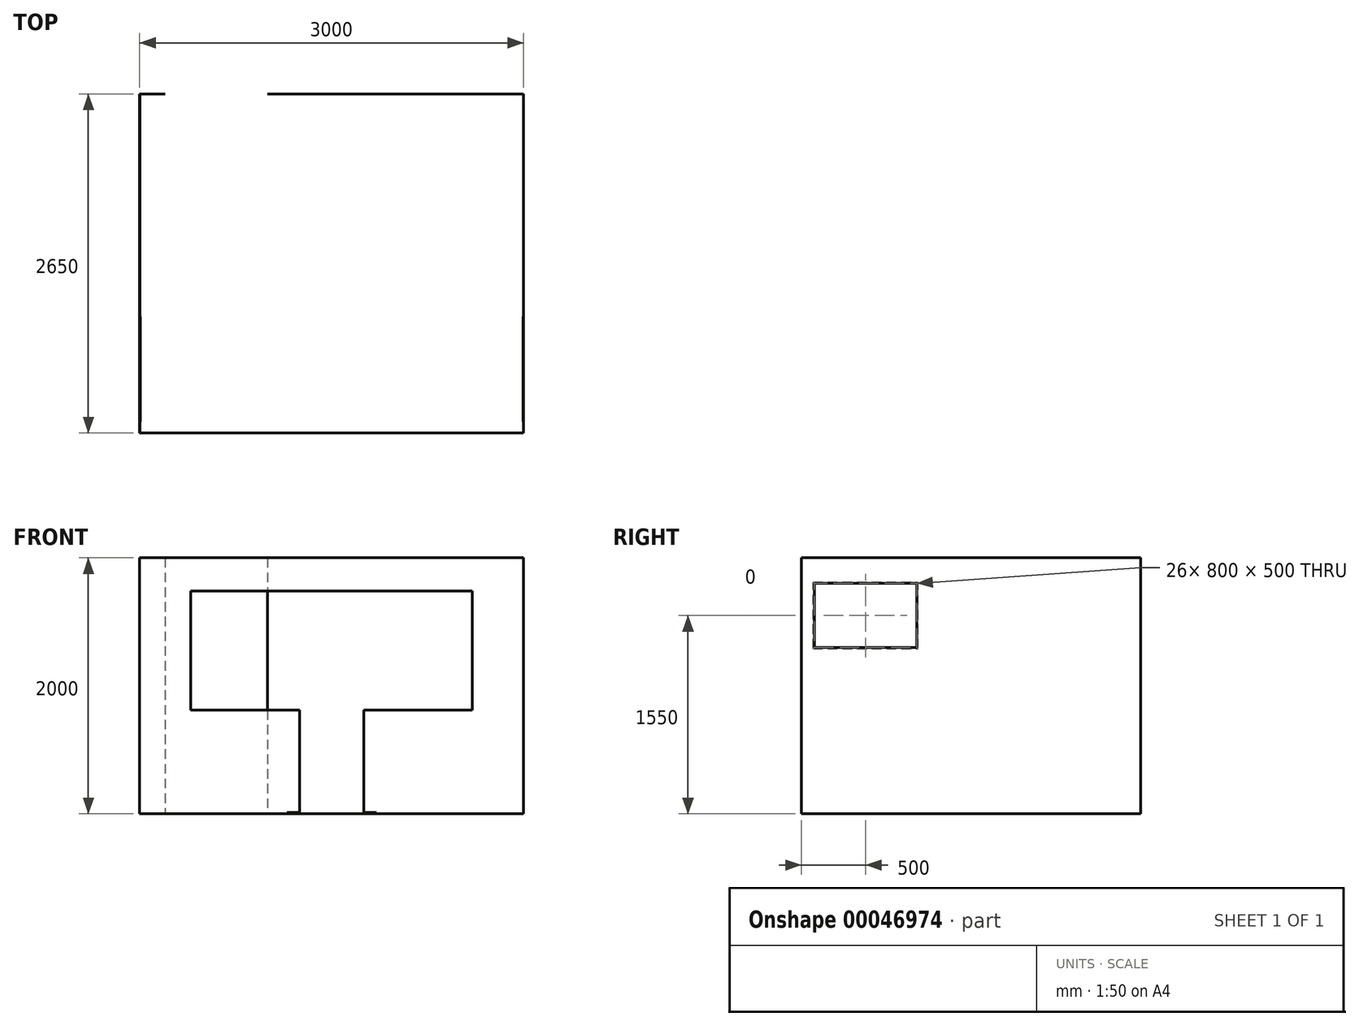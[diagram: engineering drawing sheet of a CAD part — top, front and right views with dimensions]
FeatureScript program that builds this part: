
annotation { "Feature Type Name" : "Feature", "Feature Type Description" : "" }
export const myFeature = defineFeature(function(context is Context, id is Id, definition is map)
    precondition{}
    {
        {
            var Q0;
            Q0=qCreatedBy(makeId("Top.planeOp"),FACE);
            var sketch = newSketch(context, id + "F0", { "sketchPlane" : qUnion([Q0])});
            skLineSegment(sketch, "E0.rect.bottom", {"start": v(-1500, 1325) * mm, "end": v(1500, 1325) * mm});
            skLineSegment(sketch, "E0.rect.top", {"start": v(-1500, -1325) * mm, "end": v(1500, -1325) * mm});
            skLineSegment(sketch, "E0.rect.left", {"start": v(-1500, 1325) * mm, "end": v(-1500, -1325) * mm});
            skLineSegment(sketch, "E0.rect.right", {"start": v(1500, 1325) * mm, "end": v(1500, -1325) * mm});
            skPoint(sketch, "E0.rect.middle", {"position": v(0, 0) * mm});
            skLineSegment(sketch, "E1.0", {"start": v(-1498, 1323) * mm, "end": v(-1498, -1323) * mm});
            skLineSegment(sketch, "E1.1", {"start": v(-1498, 1323) * mm, "end": v(1498, 1323) * mm});
            skLineSegment(sketch, "E1.2", {"start": v(1498, 1323) * mm, "end": v(1498, -1323) * mm});
            skLineSegment(sketch, "E1.3", {"start": v(-1498, -1323) * mm, "end": v(1498, -1323) * mm});
            skLineSegment(sketch, "E2", {"start": v(0, 1323) * mm, "end": v(0, -1323) * mm, "construction": true});
            skSolve(sketch);
        }
        {
            var Q0;
            Q0=qSketchRegion(id+"F0",true);
            extrude(context, id + "F1", {"entities" : qUnion([Q0]), "depth" : 2000 * mm});
        }
        {
            var Q0;
            Q0=makeQuery(id+"F1.opExtrude","SWEPT_FACE",FACE,{"disambiguationData":[OSD([sQuery(id+"F0.wireOp",EDGE,"E0.rect.top")])]});
            var sketch = newSketch(context, id + "F2", { "sketchPlane" : qUnion([Q0])});
            skLineSegment(sketch, "E3", {"start": v(0, 0) * mm, "end": v(0, 1740) * mm, "construction": true});
            skLineSegment(sketch, "E4", {"start": v(0, 1740) * mm, "end": v(-1100, 1740) * mm});
            skLineSegment(sketch, "E5", {"start": v(-1100, 0) * mm, "end": v(0, 0) * mm});
            skLineSegment(sketch, "E6.MirrorCS", {"start": v(1100, 0) * mm, "end": v(0, 0) * mm});
            skLineSegment(sketch, "E7.MirrorCS", {"start": v(0, 1740) * mm, "end": v(1100, 1740) * mm});
            skLineSegment(sketch, "E8", {"start": v(-1100, 810) * mm, "end": v(-350, 810) * mm});
            skLineSegment(sketch, "E9", {"start": v(-1100, 810) * mm, "end": v(-1100, 1740) * mm});
            skLineSegment(sketch, "E10.MirrorCS", {"start": v(1100, 810) * mm, "end": v(1100, 1740) * mm});
            skLineSegment(sketch, "E11", {"start": v(350, 10) * mm, "end": v(250, 10) * mm});
            skLineSegment(sketch, "E12", {"start": v(250, 10) * mm, "end": v(250, 810) * mm});
            skLineSegment(sketch, "E13", {"start": v(350, 10) * mm, "end": v(350, 0) * mm});
            skLineSegment(sketch, "E14.MirrorCS", {"start": v(-350, 10) * mm, "end": v(-350, 0) * mm});
            skLineSegment(sketch, "E15.MirrorCS", {"start": v(-350, 810) * mm, "end": v(-250, 810) * mm});
            skLineSegment(sketch, "E16.MirrorCS", {"start": v(-250, 10) * mm, "end": v(-250, 810) * mm});
            skLineSegment(sketch, "E17.MirrorCS", {"start": v(-350, 10) * mm, "end": v(-250, 10) * mm});
            skLineSegment(sketch, "E18", {"start": v(1100, 810) * mm, "end": v(250, 810) * mm});
            skSolve(sketch);
        }
        {
            var Q0;
            Q0=qSketchRegion(id+"F2",true);
            extrude(context, id + "F3", {"entities" : qUnion([Q0]), "operationType" : NewBodyOperationType.REMOVE, "oppositeDirection" : true, "depth" : 2 * mm});
        }
        {
            var Q0;
            Q0=makeQuery(id+"F1.opExtrude","SWEPT_FACE",FACE,{"disambiguationData":[OSD([sQuery(id+"F0.wireOp",EDGE,"E0.rect.left")])]});
            var sketch = newSketch(context, id + "F4", { "sketchPlane" : qUnion([Q0])});
            skLineSegment(sketch, "E19.rect.bottom", {"start": v(425, 1300) * mm, "end": v(1225, 1300) * mm});
            skLineSegment(sketch, "E19.rect.top", {"start": v(425, 1800) * mm, "end": v(1225, 1800) * mm});
            skLineSegment(sketch, "E19.rect.left", {"start": v(425, 1300) * mm, "end": v(425, 1800) * mm});
            skLineSegment(sketch, "E19.rect.right", {"start": v(1225, 1300) * mm, "end": v(1225, 1800) * mm});
            skPoint(sketch, "E19.rect.middle", {"position": v(825, 1550) * mm});
            skSolve(sketch);
        }
        {
            var Q0;
            Q0=makeQuery(id+"F1.opExtrude","SWEPT_FACE",FACE,{"disambiguationData":[OSD([sQuery(id+"F0.wireOp",EDGE,"E0.rect.right")])]});
            var sketch = newSketch(context, id + "F5", { "sketchPlane" : qUnion([Q0])});
            skLineSegment(sketch, "E20.rect.bottom", {"start": v(-1225, 1300) * mm, "end": v(-425, 1300) * mm});
            skLineSegment(sketch, "E20.rect.top", {"start": v(-1225, 1800) * mm, "end": v(-425, 1800) * mm});
            skLineSegment(sketch, "E20.rect.left", {"start": v(-1225, 1300) * mm, "end": v(-1225, 1800) * mm});
            skLineSegment(sketch, "E20.rect.right", {"start": v(-425, 1300) * mm, "end": v(-425, 1800) * mm});
            skPoint(sketch, "E20.rect.middle", {"position": v(-825, 1550) * mm});
            skSolve(sketch);
        }
        {
            var Q0;
            Q0=makeQuery(id+"F4.imprint","IMPRINT",FACE,{"disambiguationData":[TD([[makeQuery(id+"F4.imprint","IMPRINT",EDGE,{"derivedFrom":sQuery(id+"F4.wireOp",EDGE,"E19.rect.bottom")}),1.0]])]});
            extrude(context, id + "F6", {"entities" : qUnion([Q0]), "operationType" : NewBodyOperationType.REMOVE, "oppositeDirection" : true, "depth" : 2 * mm});
        }
        {
            var Q0;
            Q0=makeQuery(id+"F5.imprint","IMPRINT",FACE,{"disambiguationData":[TD([[makeQuery(id+"F5.imprint","IMPRINT",EDGE,{"derivedFrom":sQuery(id+"F5.wireOp",EDGE,"E20.rect.bottom")}),1.0]])]});
            extrude(context, id + "F7", {"entities" : qUnion([Q0]), "operationType" : NewBodyOperationType.REMOVE, "oppositeDirection" : true, "depth" : 2 * mm});
        }
        {
            var Q0;
            Q0=makeQuery(id+"F1.opExtrude","SWEPT_FACE",FACE,{"disambiguationData":[OSD([sQuery(id+"F0.wireOp",EDGE,"E1.2")])]});
            var sketch = newSketch(context, id + "F8", { "sketchPlane" : qUnion([Q0])});
            skLineSegment(sketch, "E21.rect.bottom", {"start": v(415, 1290) * mm, "end": v(1235, 1290) * mm});
            skLineSegment(sketch, "E21.rect.top", {"start": v(415, 1810) * mm, "end": v(1235, 1810) * mm});
            skLineSegment(sketch, "E21.rect.left", {"start": v(415, 1290) * mm, "end": v(415, 1810) * mm});
            skLineSegment(sketch, "E21.rect.right", {"start": v(1235, 1290) * mm, "end": v(1235, 1810) * mm});
            skPoint(sketch, "E21.rect.middle", {"position": v(825, 1550) * mm});
            skSolve(sketch);
        }
        {
            var Q0;
            Q0=qSketchRegion(id+"F8",true);
            extrude(context, id + "F9", {"entities" : qUnion([Q0]), "depth" : 2 * mm});
        }
        {
            var Q0;
            Q0=makeQuery(id+"F1.opExtrude","SWEPT_FACE",FACE,{"disambiguationData":[OSD([sQuery(id+"F0.wireOp",EDGE,"E1.0")])]});
            var sketch = newSketch(context, id + "F10", { "sketchPlane" : qUnion([Q0])});
            skLineSegment(sketch, "E22.rect.bottom", {"start": v(-1235, 1290) * mm, "end": v(-415, 1290) * mm});
            skLineSegment(sketch, "E22.rect.top", {"start": v(-1235, 1810) * mm, "end": v(-415, 1810) * mm});
            skLineSegment(sketch, "E22.rect.left", {"start": v(-1235, 1290) * mm, "end": v(-1235, 1810) * mm});
            skLineSegment(sketch, "E22.rect.right", {"start": v(-415, 1290) * mm, "end": v(-415, 1810) * mm});
            skPoint(sketch, "E22.rect.middle", {"position": v(-825, 1550) * mm});
            skSolve(sketch);
        }
        {
            var Q0;
            Q0=qSketchRegion(id+"F10",true);
            extrude(context, id + "F11", {"entities" : qUnion([Q0]), "depth" : 2 * mm});
        }
        {
            var Q0;
            Q0=makeQuery(id+"F1.opExtrude","SWEPT_FACE",FACE,{"disambiguationData":[OSD([sQuery(id+"F0.wireOp",EDGE,"E0.rect.bottom")])]});
            var sketch = newSketch(context, id + "F12", { "sketchPlane" : qUnion([Q0])});
            skLineSegment(sketch, "E23.bottom", {"start": v(500, 2000) * mm, "end": v(1300, 2000) * mm});
            skLineSegment(sketch, "E23.top", {"start": v(500, 0) * mm, "end": v(1300, 0) * mm});
            skLineSegment(sketch, "E23.left", {"start": v(500, 2000) * mm, "end": v(500, 0) * mm});
            skLineSegment(sketch, "E23.right", {"start": v(1300, 2000) * mm, "end": v(1300, 0) * mm});
            skSolve(sketch);
        }
        {
            var Q0;
            Q0=makeQuery(id+"F12.imprint","IMPRINT",FACE,{"disambiguationData":[TD([[makeQuery(id+"F12.imprint","IMPRINT",EDGE,{"derivedFrom":sQuery(id+"F12.wireOp",EDGE,"E23.bottom")}),1.0]])]});
            extrude(context, id + "F13", {"entities" : qUnion([Q0]), "operationType" : NewBodyOperationType.REMOVE, "oppositeDirection" : true, "depth" : 2 * mm});
        }
        {
            var Q0;
            {var subQ0=sQuery(id+"F0.wireOp",EDGE,"E0.rect.bottom");var subQ1=sQuery(id+"F0.wireOp",EDGE,"E0.rect.right");Q0=makeQuery(id+"F13.boolean.opBoolean","SPLIT",FACE,{"disambiguationData":[TD([makeQuery(id+"F1.opExtrude","SWEPT_FACE",FACE,{"disambiguationData":[OSD([subQ1])]})])],"derivedFrom":makeQuery(id+"F1.opExtrude","SWEPT_FACE",FACE,{"disambiguationData":[OSD([subQ0])]})});}
            var sketch = newSketch(context, id + "F14", { "sketchPlane" : qUnion([Q0])});
            skLineSegment(sketch, "E24", {"start": v(-1500, 0) * mm, "end": v(-1400, 0) * mm, "construction": true});
            skSolve(sketch);
        }
    });
